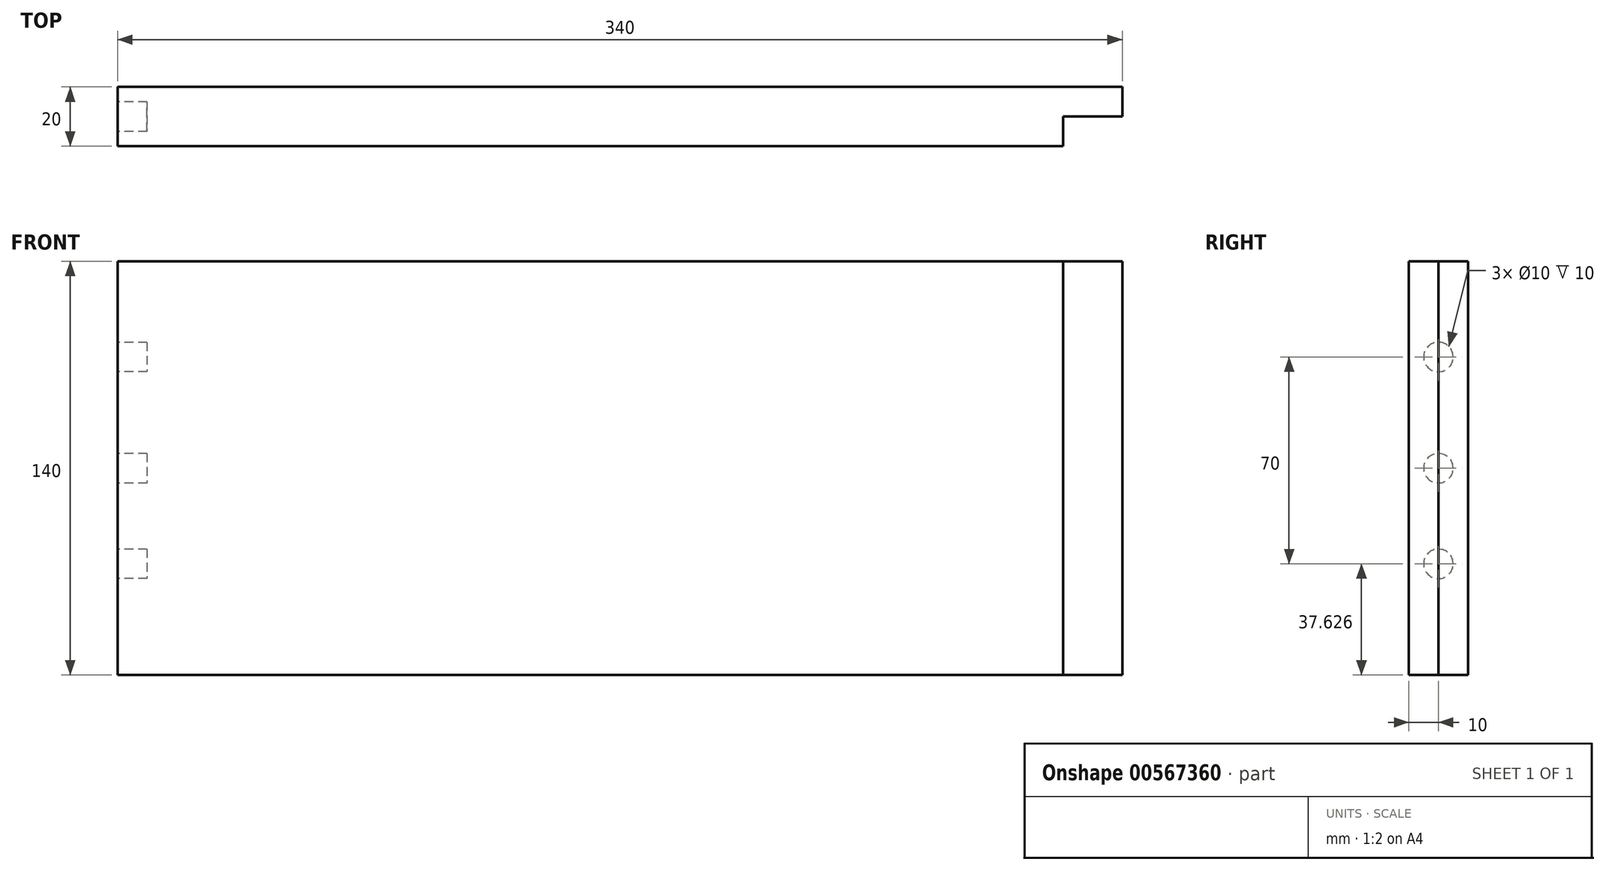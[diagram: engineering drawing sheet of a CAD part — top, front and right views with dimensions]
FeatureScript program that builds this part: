
annotation { "Feature Type Name" : "Feature", "Feature Type Description" : "" }
export const myFeature = defineFeature(function(context is Context, id is Id, definition is map)
    precondition{}
    {
        {
            var Q0;
            Q0=qCreatedBy(makeId("Front.planeOp"),FACE);
            var sketch = newSketch(context, id + "F0", { "sketchPlane" : qUnion([Q0])});
            skLineSegment(sketch, "E0.bottom", {"start": v(-340, 140) * mm, "end": v(0, 140) * mm});
            skLineSegment(sketch, "E0.top", {"start": v(-340, 0) * mm, "end": v(0, 0) * mm});
            skLineSegment(sketch, "E0.left", {"start": v(-340, 140) * mm, "end": v(-340, 0) * mm});
            skLineSegment(sketch, "E0.right", {"start": v(0, 140) * mm, "end": v(0, 0) * mm});
            skLineSegment(sketch, "E1.bottom", {"start": v(-340, 140) * mm, "end": v(-320, 140) * mm});
            skLineSegment(sketch, "E1.top", {"start": v(-340, 0) * mm, "end": v(-320, 0) * mm});
            skLineSegment(sketch, "E1.right", {"start": v(-320, 140) * mm, "end": v(-320, 0) * mm});
            skSolve(sketch);
        }
        {
            var Q0;
            Q0 = qSketchRegion(id + "F0", true);
            var Q1;
            Q1=makeQuery(id+"F0.imprint","IMPRINT",FACE,{"disambiguationData":[TD([[makeQuery(id+"F0.imprint","IMPRINT",EDGE,{"derivedFrom":sQuery(id+"F0.wireOp",EDGE,"E0.bottom")}),-1.0]])]});
            extrude(context, id + "F1", {"entities" : qUnion([Q0, Q1]), "depth" : 20 * mm, "offsetDistance" : 25 * mm});
        }
        {
            var Q0;
            Q0=makeQuery(id+"F1.opExtrude","SWEPT_FACE",FACE,{"disambiguationData":[OSD([sQuery(id+"F0.wireOp",EDGE,"E0.right")])]});
            var sketch = newSketch(context, id + "F2", { "sketchPlane" : qUnion([Q0])});
            skLineSegment(sketch, "E2.bottom", {"start": v(-20, 140) * mm, "end": v(-10, 140) * mm});
            skLineSegment(sketch, "E2.top", {"start": v(-20, 0) * mm, "end": v(-10, 0) * mm});
            skLineSegment(sketch, "E2.left", {"start": v(-20, 140) * mm, "end": v(-20, 0) * mm});
            skLineSegment(sketch, "E2.right", {"start": v(-10, 140) * mm, "end": v(-10, 0) * mm});
            skSolve(sketch);
        }
        {
            var Q0;
            Q0=makeQuery(id+"F2.imprint","IMPRINT",FACE,{"disambiguationData":[TD([[makeQuery(id+"F2.imprint","IMPRINT",EDGE,{"derivedFrom":sQuery(id+"F2.wireOp",EDGE,"E2.bottom")}),-1.0]])]});
            extrude(context, id + "F3", {"entities" : qUnion([Q0]), "operationType" : NewBodyOperationType.REMOVE, "oppositeDirection" : true, "depth" : 20 * mm, "offsetDistance" : 25 * mm});
        }
        {
            var Q0;
            Q0=makeQuery(id+"F1.opExtrude","SWEPT_FACE",FACE,{"disambiguationData":[OSD([sQuery(id+"F0.wireOp",EDGE,"E0.left")])]});
            var sketch = newSketch(context, id + "F4", { "sketchPlane" : qUnion([Q0])});
            skLineSegment(sketch, "E3.bottom", {"start": v(0, 140) * mm, "end": v(20, 140) * mm});
            skLineSegment(sketch, "E3.left", {"start": v(0, 140) * mm, "end": v(0, 75.25) * mm});
            skLineSegment(sketch, "E3.right", {"start": v(20, 140) * mm, "end": v(20, 75.25) * mm});
            skLineSegment(sketch, "E4.bottom", {"start": v(20, 0) * mm, "end": v(0, 0) * mm});
            skLineSegment(sketch, "E4.right", {"start": v(0, 0) * mm, "end": v(0, 75.25) * mm});
            skLineSegment(sketch, "E5", {"start": v(20, 140) * mm, "end": v(20, 70) * mm});
            skLineSegment(sketch, "E6", {"start": v(20, 70) * mm, "end": v(0, 70) * mm});
            skLineSegment(sketch, "E7", {"start": v(0, 70) * mm, "end": v(0, 107.63) * mm});
            skLineSegment(sketch, "E8", {"start": v(0, 107.63) * mm, "end": v(20, 107.63) * mm});
            skLineSegment(sketch, "E9", {"start": v(0, 70) * mm, "end": v(0, 37.63) * mm});
            skLineSegment(sketch, "E10", {"start": v(0, 37.63) * mm, "end": v(20, 37.63) * mm});
            skCircle(sketch, "E11", {"center": v(10, 107.63) * mm, "radius": 5 * mm});
            skCircle(sketch, "E12", {"center": v(10, 70) * mm, "radius": 5 * mm});
            skCircle(sketch, "E13", {"center": v(10, 37.63) * mm, "radius": 5 * mm});
            skSolve(sketch);
        }
        {
            var Q0;
            {var subQ0=sQuery(id+"F4.wireOp",EDGE,"E13");var subQ1=sQuery(id+"F4.wireOp",EDGE,"E10");var subQ2=makeQuery(id+"F4.imprint","INTERSECT",VERTEX,{"disambiguationData":[OD(0.0)],"derivedFrom":[subQ1,subQ0]});Q0=makeQuery(id+"F4.imprint","IMPRINT",FACE,{"disambiguationData":[TD([[makeQuery(id+"F4.imprint","IMPRINT",EDGE,{"disambiguationData":[TD([[subQ2,-1.0]])],"derivedFrom":subQ1}),1.0]])]});}
            var Q1;
            {var subQ0=sQuery(id+"F4.wireOp",EDGE,"E13");var subQ1=sQuery(id+"F4.wireOp",EDGE,"E10");var subQ2=makeQuery(id+"F4.imprint","INTERSECT",VERTEX,{"disambiguationData":[OD(0.0)],"derivedFrom":[subQ1,subQ0]});Q1=makeQuery(id+"F4.imprint","IMPRINT",FACE,{"disambiguationData":[TD([[makeQuery(id+"F4.imprint","IMPRINT",EDGE,{"disambiguationData":[TD([[subQ2,-1.0]])],"derivedFrom":subQ1}),-1.0]])]});}
            var Q2;
            {var subQ0=sQuery(id+"F4.wireOp",EDGE,"E11");var subQ1=sQuery(id+"F4.wireOp",EDGE,"E8");var subQ2=makeQuery(id+"F4.imprint","INTERSECT",VERTEX,{"disambiguationData":[OD(0.0)],"derivedFrom":[subQ1,subQ0]});Q2=makeQuery(id+"F4.imprint","IMPRINT",FACE,{"disambiguationData":[TD([[makeQuery(id+"F4.imprint","IMPRINT",EDGE,{"disambiguationData":[TD([[subQ2,-1.0]])],"derivedFrom":subQ1}),1.0]])]});}
            var Q3;
            {var subQ0=sQuery(id+"F4.wireOp",EDGE,"E11");var subQ1=sQuery(id+"F4.wireOp",EDGE,"E8");var subQ2=makeQuery(id+"F4.imprint","INTERSECT",VERTEX,{"disambiguationData":[OD(0.0)],"derivedFrom":[subQ1,subQ0]});Q3=makeQuery(id+"F4.imprint","IMPRINT",FACE,{"disambiguationData":[TD([[makeQuery(id+"F4.imprint","IMPRINT",EDGE,{"disambiguationData":[TD([[subQ2,-1.0]])],"derivedFrom":subQ1}),-1.0]])]});}
            var Q4;
            {var subQ0=sQuery(id+"F4.wireOp",EDGE,"E12");var subQ1=sQuery(id+"F4.wireOp",EDGE,"E6");var subQ2=makeQuery(id+"F4.imprint","INTERSECT",VERTEX,{"disambiguationData":[OD(0.0)],"derivedFrom":[subQ1,subQ0]});Q4=makeQuery(id+"F4.imprint","IMPRINT",FACE,{"disambiguationData":[TD([[makeQuery(id+"F4.imprint","IMPRINT",EDGE,{"disambiguationData":[TD([[subQ2,-1.0]])],"derivedFrom":subQ1}),1.0]])]});}
            var Q5;
            {var subQ0=sQuery(id+"F4.wireOp",EDGE,"E12");var subQ1=sQuery(id+"F4.wireOp",EDGE,"E6");var subQ2=makeQuery(id+"F4.imprint","INTERSECT",VERTEX,{"disambiguationData":[OD(0.0)],"derivedFrom":[subQ1,subQ0]});Q5=makeQuery(id+"F4.imprint","IMPRINT",FACE,{"disambiguationData":[TD([[makeQuery(id+"F4.imprint","IMPRINT",EDGE,{"disambiguationData":[TD([[subQ2,-1.0]])],"derivedFrom":subQ1}),-1.0]])]});}
            extrude(context, id + "F5", {"entities" : qUnion([Q0, Q1, Q2, Q3, Q4, Q5]), "operationType" : NewBodyOperationType.REMOVE, "oppositeDirection" : true, "depth" : 10 * mm, "offsetDistance" : 25 * mm});
        }
    });
